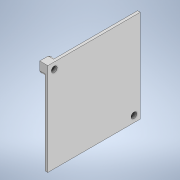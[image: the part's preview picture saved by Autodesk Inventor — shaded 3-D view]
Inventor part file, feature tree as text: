
AUTODESK INVENTOR PART (.ipt)
format: ipt  version: 2021 (Build 250183000, 183)  size: 138,752 bytes
history: native  units: mm
features: extrude x4, sketch x3, pattern_circular x1, projected_geometry x1
ambient origin geometry x8: Origin, YZ Plane, XZ Plane, XY Plane, X Axis, Y Axis, Z Axis, Center Point
bodies: Solid1 (feature_tree)
feature tree (9):
  extrude  "Extrusion1"  Depth=69.0mm
  sketch  "Sketch2"  dims[d2=2.0mm d3=0.0mm d4=7.5mm]
  extrude  "Extrusion2"  Depth=2.0mm
  extrude  "Extrusion3"  Depth=5.0mm
  pattern_circular  "Circular Pattern1"  [2 undecoded]
  extrude  "Extrusion4"  Depth=4.0mm TaperAngle=0.0deg
  sketch  "Sketch1"  dims[d0=69.0mm d1=69.0mm]
  sketch  "Sketch3"  dims[d5=10.0mm d6=5.0mm d7=5.0mm d8=4.0mm d9=0.0mm d10=4.3mm d11=4.0mm d12=0.0mm d13=20.0mm d14=360.0deg d16=0.25mm d17=0.25mm d18=0.0mm d19=0.0mm]
  projected_geometry  "Projected Loop1"
note: 2 required parameter values undecoded (feature->parameter linkage not recoverable at this tier; creation-order binding heuristic only, values carry confidence <= 0.55)
